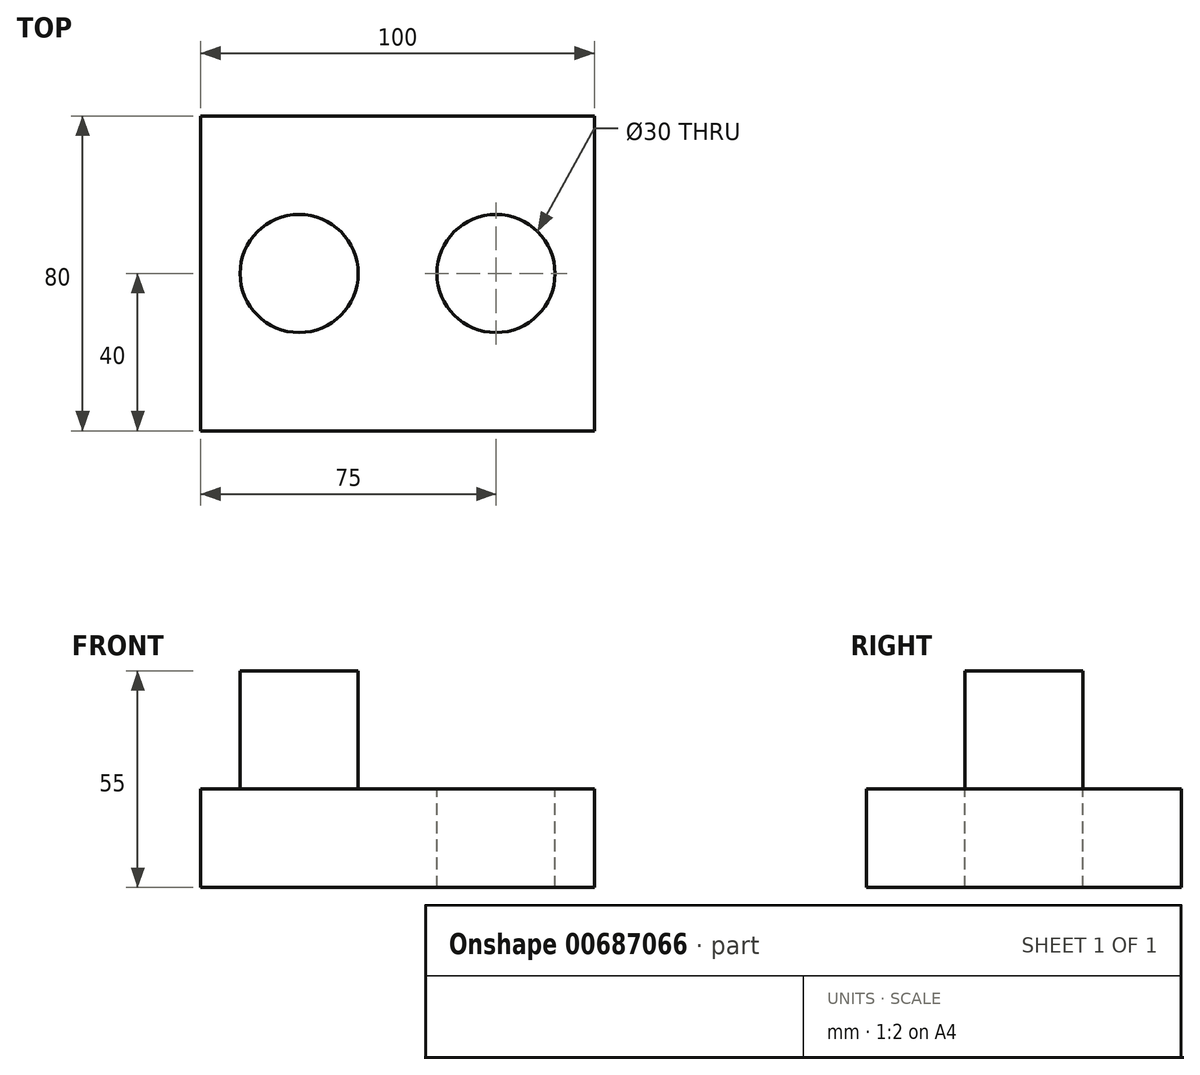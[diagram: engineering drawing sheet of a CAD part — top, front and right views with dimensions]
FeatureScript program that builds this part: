
annotation { "Feature Type Name" : "Feature", "Feature Type Description" : "" }
export const myFeature = defineFeature(function(context is Context, id is Id, definition is map)
    precondition{}
    {
        {
            var Q0;
            Q0=qCreatedBy(makeId("Top.planeOp"),FACE);
            var sketch = newSketch(context, id + "F0", { "sketchPlane" : qUnion([Q0])});
            skLineSegment(sketch, "E0.bottom", {"start": v(50, -40) * mm, "end": v(-50, -40) * mm});
            skLineSegment(sketch, "E0.top", {"start": v(50, 40) * mm, "end": v(-50, 40) * mm});
            skLineSegment(sketch, "E0.left", {"start": v(50, -40) * mm, "end": v(50, 40) * mm});
            skLineSegment(sketch, "E0.right", {"start": v(-50, -40) * mm, "end": v(-50, 40) * mm});
            skPoint(sketch, "E0.middle", {"position": v(0, 0) * mm});
            skSolve(sketch);
        }
        {
            var Q0;
            Q0 = qSketchRegion(id + "F0", true);
            extrude(context, id + "F1", {"entities" : qUnion([Q0]), "depth" : 25 * mm, "offsetDistance" : 25 * mm});
        }
        {
            var Q0;
            Q0=makeQuery(id+"F1.opExtrude","CAP_FACE",FACE,{"disambiguationData":[OSD([sQuery(id+"F0.wireOp",EDGE,"E0.bottom"),sQuery(id+"F0.wireOp",EDGE,"E0.top"),sQuery(id+"F0.wireOp",EDGE,"E0.left"),sQuery(id+"F0.wireOp",EDGE,"E0.right")])],"isStart":false});
            var sketch = newSketch(context, id + "F2", { "sketchPlane" : qUnion([Q0])});
            skCircle(sketch, "E1", {"center": v(-25, 0) * mm, "radius": 15 * mm});
            skSolve(sketch);
        }
        {
            var Q0;
            Q0 = qSketchRegion(id + "F2", true);
            extrude(context, id + "F3", {"entities" : qUnion([Q0]), "operationType" : NewBodyOperationType.ADD, "depth" : 30 * mm, "offsetDistance" : 25 * mm});
        }
        {
            var Q0;
            Q0=makeQuery(id+"F1.opExtrude","CAP_FACE",FACE,{"disambiguationData":[OSD([sQuery(id+"F0.wireOp",EDGE,"E0.bottom"),sQuery(id+"F0.wireOp",EDGE,"E0.top"),sQuery(id+"F0.wireOp",EDGE,"E0.left"),sQuery(id+"F0.wireOp",EDGE,"E0.right")])],"isStart":false});
            var sketch = newSketch(context, id + "F4", { "sketchPlane" : qUnion([Q0])});
            skCircle(sketch, "E2", {"center": v(25, 0) * mm, "radius": 15 * mm});
            skSolve(sketch);
        }
        {
            var Q0;
            Q0 = qSketchRegion(id + "F4", true);
            extrude(context, id + "F5", {"entities" : qUnion([Q0]), "operationType" : NewBodyOperationType.REMOVE, "oppositeDirection" : true, "depth" : 25 * mm, "offsetDistance" : 25 * mm});
        }
    });
